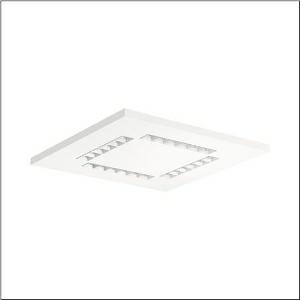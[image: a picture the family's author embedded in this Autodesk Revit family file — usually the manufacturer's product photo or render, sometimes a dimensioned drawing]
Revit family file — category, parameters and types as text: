
# Revit family: silica_r__21_square_51mx6nds44w_aabb
name_source: partatom
category: Lighting Fixtures
units: mm (PartAtom-declared; Revit-internal decimal feet)

## family parameters
Cut with Voids When Loaded = No
Host = Face
Light Source = No
Part Type = Normal
Room Calculation Point = No
Round Connector Dimension = Use Diameter
Shared = No

## types (1)
- --- (1 x LED, 4600 lm, 27 W, 4000K)
    Apparent Load = 27 VA
    CIE Flux Codes = 83 98 100 100 100
    Color Rendering = 80
    Color Temperature = 4000K
    Default Elevation = 1800 mm
    Description = Silica® 21 Square, office luminaire, primary light control with lens, of PMMA, primary anti-glare with reflector, of PC, white, CAT 2 (L<= 3000cd/m²), light emission: direct distribution, primary light characteristic: symmetric, installation type: lay-in mounting, LED, rated luminous flux: 4.600lm, luminous efficacy: 170lm/W, light colour: 840, colour temperature: 4000K, control gear: DALI 2, with terminal, 5-pole, mains connection: 220..240V, AC, 50/60Hz, rated input power: 27W, luminaire housing, of aluminium, traffic white (RAL 9016), module: M600, length: 600mm, width: 600mm, height: 32mm, protection rating (complete): IP20, insulation class (complete): insulation class I (protective earthing), certification: CE, ENEC, VDE, permissible operating ambient temperature: 0..+35°C, standard: EN 50419, packaging unit: 1 piece
    Height = 0 mm  [stored 0 ft]
    Lamp = 1 x LED
    Lamp Light Flux = 4600 lm
    Lamp Power = 27 W
    Lamp count = 1
    Length = 597 mm
    Luminous efficacy = 170 lm/W
    Manufacturer = Siteco
    ModVariant = No
    Model = 51MX6NDS44W
    Mounting Place = Ceiling
    Mounting Type = Recessed
    Number of Poles = 1
    OnlyDefault = Yes
    Power Factor = 1
    Product Name = Silica® 21 Square
    Product group = office luminaire | ceiling recessed
    ProductGroupID = 401
    Protection Class = Protection class I
    Protection Degree = IP 20
    RLX_Detail_Level = 1
    RLX_Emergency_Light_Flux = 0 lm
    RLX_Emergency_Type = 0
    RLX_Emergency_Type_DB = No
    RlxData = <blob elided: 19005 chars, md5=924eaae2>
    Socket = socket
    Standby Power = 0 W
    System Light Flux = 4600 lm
    System Power = 27 W
    Type Comments = factory setting: luminous flux: 100 % | dim-lin: 254 | 366 mA
    Type Image = l_1275224.jpg
    URL = http://relux.com
    VarID = @adj_083404
    Voltage = 0 V
    Weight = 0.00 kg
    Width = 597 mm

note: [stored X ft] marks values corroborated as IEEE doubles in the binary element streams (Revit-internal decimal feet)

## geometry (parser evidence)
native form markers: Blend x4, Sweep x10
no freeform markers — native parametric forms only
